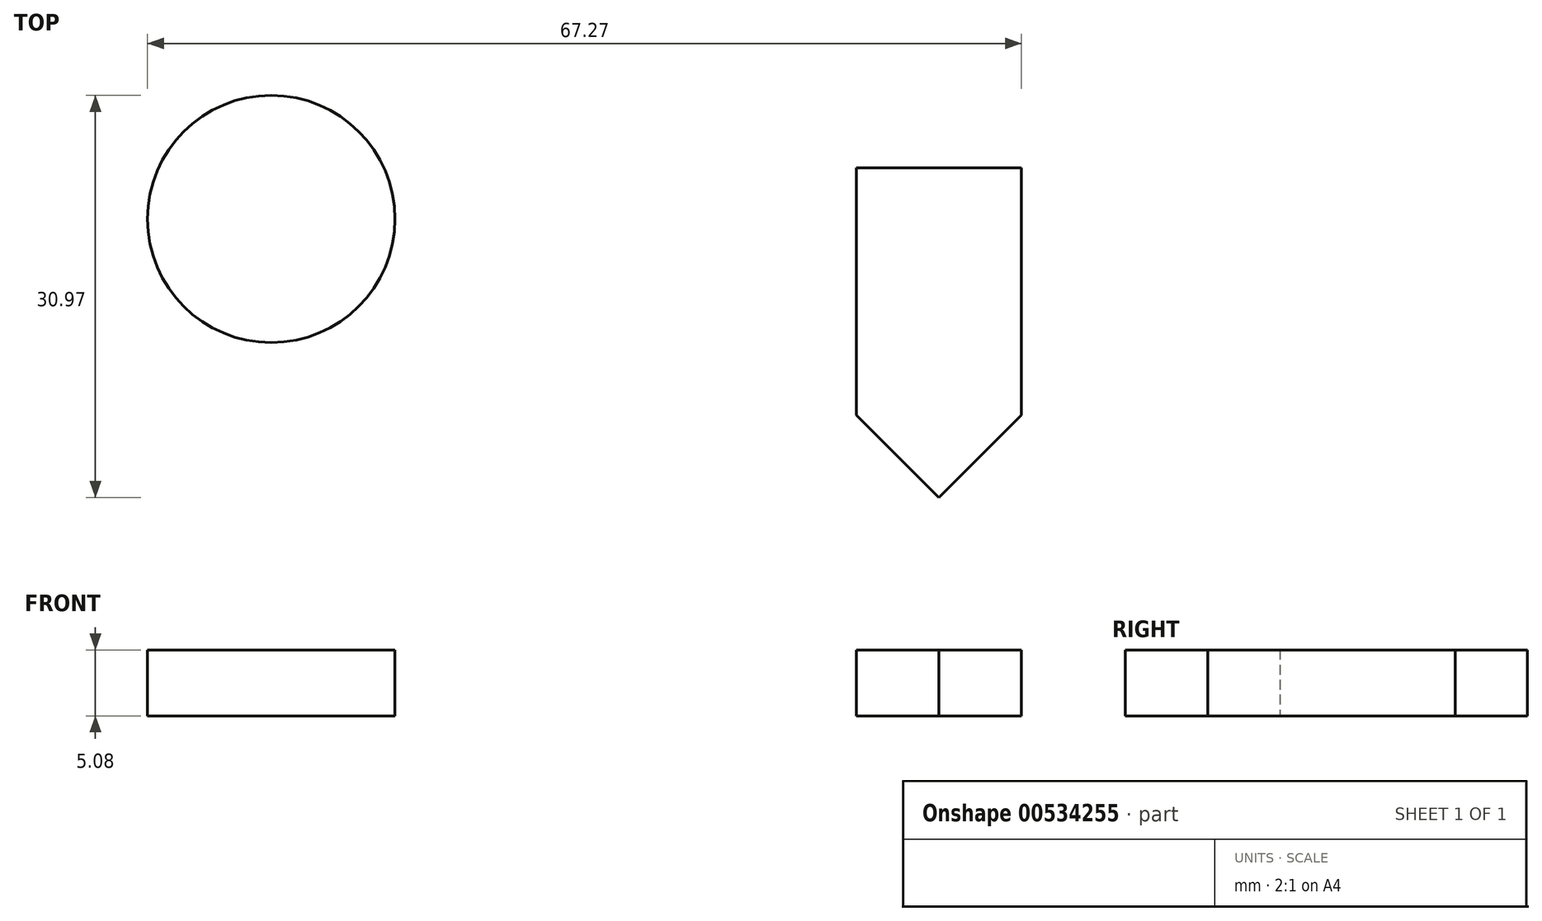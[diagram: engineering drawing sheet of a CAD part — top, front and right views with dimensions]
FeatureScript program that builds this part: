
annotation { "Feature Type Name" : "Feature", "Feature Type Description" : "" }
export const myFeature = defineFeature(function(context is Context, id is Id, definition is map)
    precondition{}
    {
        {
            var Q0;
            Q0=qCreatedBy(makeId("Top.planeOp"),FACE);
            var sketch = newSketch(context, id + "F0", { "sketchPlane" : qUnion([Q0])});
            skLineSegment(sketch, "E0.bottom", {"start": v(6.86, -9.11) * mm, "end": v(-5.84, -9.11) * mm});
            skLineSegment(sketch, "E0.top", {"start": v(6.86, 16.29) * mm, "end": v(-5.84, 16.29) * mm});
            skLineSegment(sketch, "E0.left", {"start": v(6.86, -9.11) * mm, "end": v(6.86, 16.29) * mm});
            skLineSegment(sketch, "E0.right", {"start": v(-5.84, -9.11) * mm, "end": v(-5.84, 16.29) * mm});
            skPoint(sketch, "E0.middle", {"position": v(0.5, 3.59) * mm});
            skSolve(sketch);
        }
        {
            var Q0;
            Q0=makeQuery(id+"F0.imprint","IMPRINT",FACE,{"disambiguationData":[TD([[makeQuery(id+"F0.imprint","IMPRINT",EDGE,{"derivedFrom":sQuery(id+"F0.wireOp",EDGE,"E0.bottom")}),-1.0]])]});
            extrude(context, id + "F1", {"entities" : qUnion([Q0]), "depth" : 5.08 * mm, "offsetDistance" : 25.4 * mm});
        }
        {
            var Q0;
            Q0=makeQuery(id+"F1.opExtrude","SWEPT_EDGE",EDGE,{"disambiguationData":[OSD([sQuery(id+"F0.wireOp",EDGE,"E0.bottom"),sQuery(id+"F0.wireOp",EDGE,"E0.left")])]});
            var Q1;
            Q1=makeQuery(id+"F1.opExtrude","SWEPT_EDGE",EDGE,{"disambiguationData":[OSD([sQuery(id+"F0.wireOp",EDGE,"E0.bottom"),sQuery(id+"F0.wireOp",EDGE,"E0.right")])]});
            chamfer(context, id + "F2", {"entities" : qUnion([Q0, Q1]), "width" : 6.35 * mm, "tangentPropagation" : true});
        }
        {
            var Q0;
            Q0=qCreatedBy(makeId("Top.planeOp"),FACE);
            var sketch = newSketch(context, id + "F3", { "sketchPlane" : qUnion([Q0])});
            skCircle(sketch, "E1", {"center": v(-50.88, 12.34) * mm, "radius": 9.53 * mm});
            skSolve(sketch);
        }
        {
            var Q0;
            Q0=makeQuery(id+"F3.imprint","IMPRINT",FACE,{"disambiguationData":[TD([[makeQuery(id+"F3.imprint","IMPRINT",EDGE,{"derivedFrom":sQuery(id+"F3.wireOp",EDGE,"E1")}),1.0]])]});
            extrude(context, id + "F4", {"entities" : qUnion([Q0]), "depth" : 5.08 * mm, "offsetDistance" : 25.4 * mm});
        }
    });
